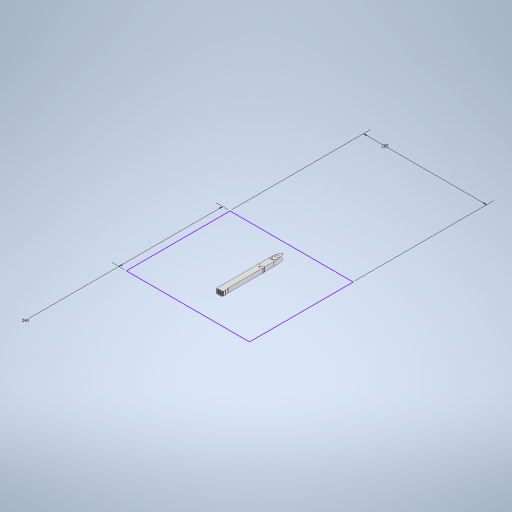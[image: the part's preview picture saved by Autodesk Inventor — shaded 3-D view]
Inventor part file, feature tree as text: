
AUTODESK INVENTOR PART (.ipt)
format: ipt  version: 2024.1 (Build 281209000, 209)  size: 622,080 bytes
history: native  units: mm
features: extrude x5, chamfer x5, sketch x2, fillet x2
ambient origin geometry x8: Origin, YZ Plane, XZ Plane, XY Plane, X Axis, Y Axis, Z Axis, Center Point
bodies: Solid1 (feature_tree), Solid2 (feature_tree), Solid3 (feature_tree), Solid4 (feature_tree), Solid5 (feature_tree)
feature tree (14):
  sketch  "Sketch3"  dims[d2=6.5mm d3=41.85mm d4=3.0mm d5=1.1mm d6=1.1mm d7=12.0mm d8=15.0mm d9=23.0mm d10=1.0mm d11=1.0mm d12=27.0mm d13=3.0mm d14=3.0mm d15=3.0mm d16=1.3mm d17=1.3mm d18=1.7mm d19=1.7mm d20=8.726646mm d21=8.726646mm d22=2.13751mm d24=2.13751mm d26=8.726646mm d28=8.726646mm d29=30.0mm d31=4.7mm d32=10.0mm d34=10.0mm d36=6.0mm d37=10.0mm d38=0.0mm d39=0.5mm d40=1.0mm d41=45.0deg d42=0.5mm d43=1.0mm d44=45.0deg d45=0.5mm d46=1.0mm d47=45.0deg d48=0.5mm d49=1.0mm d50=45.0deg d57=2.2mm d58=2.2mm d59=3.7mm d60=3.7mm d61=0.35mm d62=0.35mm d63=1.4mm d64=1.4mm d65=3.5mm d66=3.5mm d67=0.7mm d68=10.0mm d69=0.0mm d70=10.0mm d71=0.0mm d72=0.3mm d73=0.3mm d74=0.3mm d75=0.3mm d76=0.3mm d77=0.3mm d78=0.3mm d79=0.3mm d80=10.0mm d81=0.0mm d82=0.3mm d83=10.0mm d84=0.0mm d85=1.0mm d86=1.0mm d87=45.0deg d88=1.0mm d89=4.0mm d90=2.0mm d91=2.0mm d92=2.0mm d93=2.0mm d96=240.0mm d97=285.0mm]
  sketch  "Sketch1"  dims[d0=83.7mm d1=13.0mm]
  extrude  "Extrusion1"  Depth=13.0mm
  extrude  "Extrusion2"  Depth=4.0mm
  extrude  "Extrusion3"  Depth=4.0mm
  extrude  "Extrusion4"  Depth=4.0mm
  extrude  "Extrusion5"  Depth=4.0mm
  chamfer  "Chamfer1"  Distance=12.0mm
  chamfer  "Chamfer2"  Distance=15.0mm
  chamfer  "Chamfer3"  Distance=23.0mm
  chamfer  "Chamfer4"  Distance=1.0mm
  chamfer  "Chamfer5"  Distance=1.0mm
  fillet  "Fillet1"  Radius=27.0mm
  fillet  "Fillet2"  Radius=3.0mm
